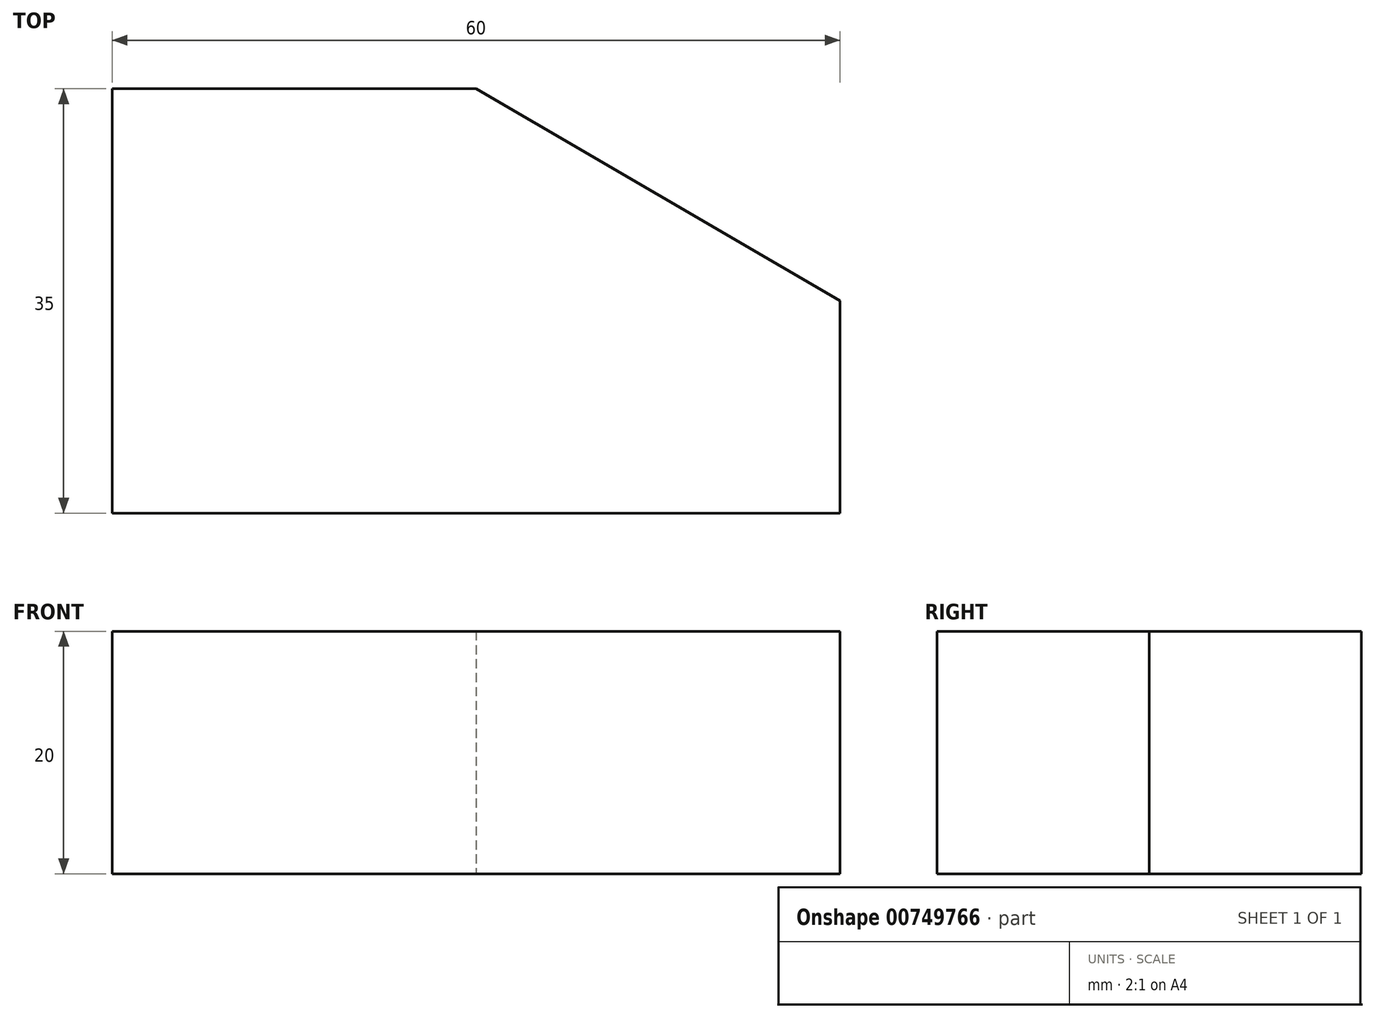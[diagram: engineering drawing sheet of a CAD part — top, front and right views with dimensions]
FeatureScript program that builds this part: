
annotation { "Feature Type Name" : "Feature", "Feature Type Description" : "" }
export const myFeature = defineFeature(function(context is Context, id is Id, definition is map)
    precondition{}
    {
        {
            var Q0;
            Q0=qCreatedBy(makeId("Top.planeOp"),FACE);
            var sketch = newSketch(context, id + "F0", { "sketchPlane" : qUnion([Q0])});
            skLineSegment(sketch, "E0.left", {"start": v(0, 0) * mm, "end": v(0, 35) * mm});
            skLineSegment(sketch, "E1", {"start": v(0, 35) * mm, "end": v(30, 35) * mm});
            skLineSegment(sketch, "E2", {"start": v(60, 0) * mm, "end": v(60, 17.5) * mm});
            skLineSegment(sketch, "E3", {"start": v(30, 35) * mm, "end": v(60, 17.5) * mm});
            skLineSegment(sketch, "E4", {"start": v(0, 0) * mm, "end": v(60, 0) * mm});
            skSolve(sketch);
        }
        {
            var Q0;
            Q0 = qSketchRegion(id + "F0", true);
            extrude(context, id + "F1", {"entities" : qUnion([Q0]), "depth" : 20 * mm, "offsetDistance" : 25 * mm});
        }
    });
